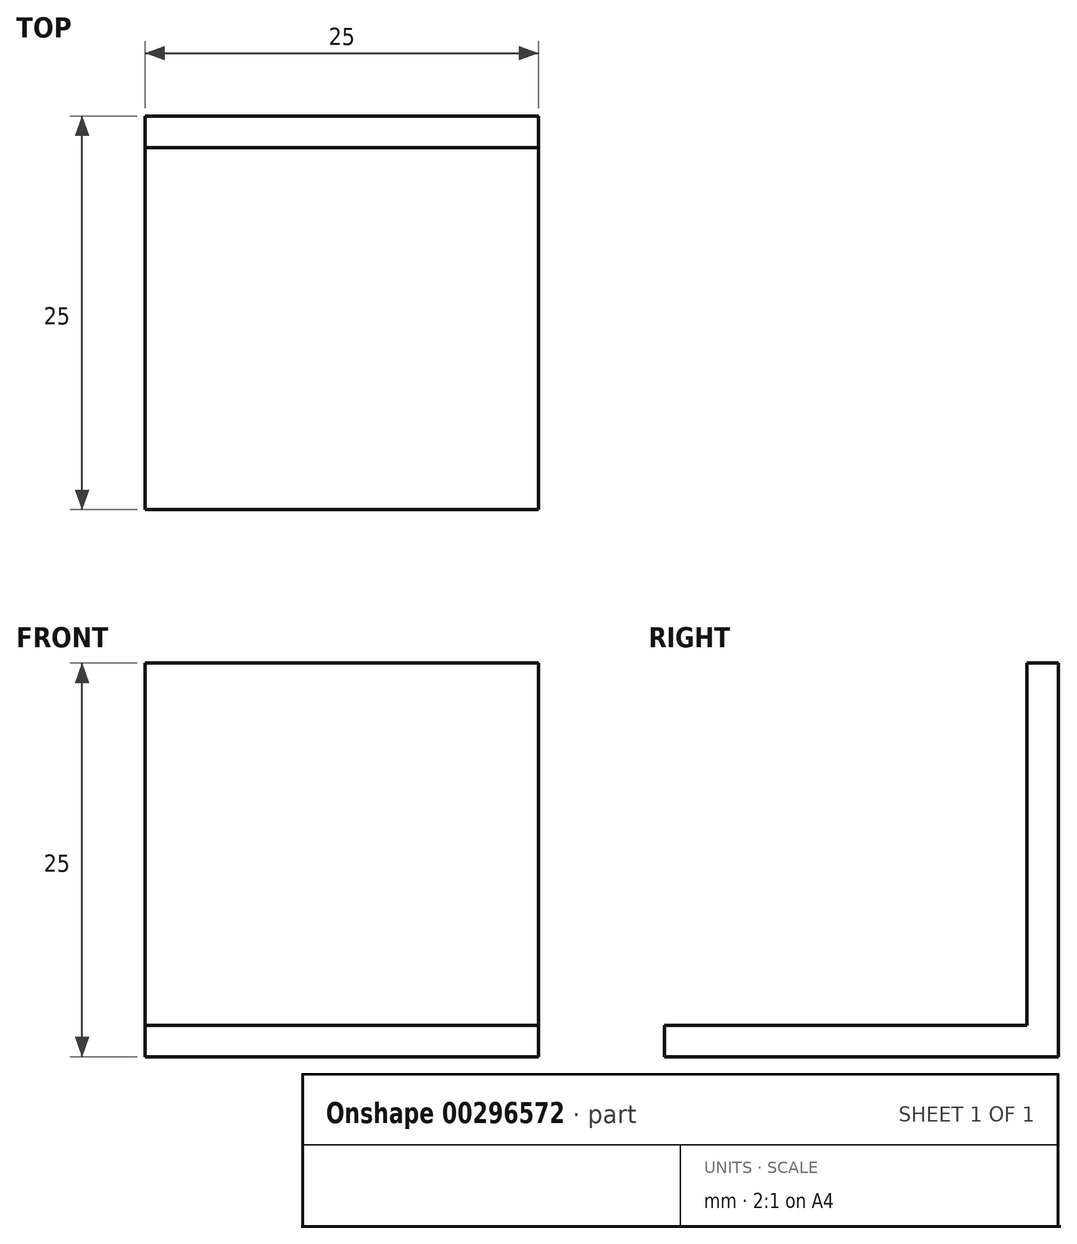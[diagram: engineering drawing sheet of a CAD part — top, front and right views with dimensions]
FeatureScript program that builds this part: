
annotation { "Feature Type Name" : "Feature", "Feature Type Description" : "" }
export const myFeature = defineFeature(function(context is Context, id is Id, definition is map)
    precondition{}
    {
        {
            var Q0;
            Q0=qCreatedBy(makeId("Top.planeOp"),FACE);
            var sketch = newSketch(context, id + "F0", { "sketchPlane" : qUnion([Q0])});
            skLineSegment(sketch, "E0.bottom", {"start": v(12.5, 12.5) * mm, "end": v(-12.5, 12.5) * mm});
            skLineSegment(sketch, "E0.top", {"start": v(12.5, -12.5) * mm, "end": v(-12.5, -12.5) * mm});
            skLineSegment(sketch, "E0.left", {"start": v(12.5, 12.5) * mm, "end": v(12.5, -12.5) * mm});
            skLineSegment(sketch, "E0.right", {"start": v(-12.5, 12.5) * mm, "end": v(-12.5, -12.5) * mm});
            skPoint(sketch, "E0.middle", {"position": v(0, 0) * mm});
            skLineSegment(sketch, "E1", {"start": v(-12.5, 10.5) * mm, "end": v(12.5, 10.5) * mm});
            skSolve(sketch);
        }
        {
            var Q0;
            {var subQ0=sQuery(id+"F0.wireOp",EDGE,"E0.top");Q0=makeQuery(id+"F0.imprint","IMPRINT",FACE,{"disambiguationData":[TD([[makeQuery(id+"F0.imprint","IMPRINT",EDGE,{"derivedFrom":subQ0}),-1.0]])]});}
            extrude(context, id + "F1", {"entities" : qUnion([Q0]), "depth" : 2 * mm});
        }
        {
            var Q0;
            {var subQ0=sQuery(id+"F0.wireOp",EDGE,"E0.bottom");Q0=makeQuery(id+"F0.imprint","IMPRINT",FACE,{"disambiguationData":[TD([[makeQuery(id+"F0.imprint","IMPRINT",EDGE,{"derivedFrom":subQ0}),1.0]])]});}
            extrude(context, id + "F2", {"entities" : qUnion([Q0]), "operationType" : NewBodyOperationType.ADD, "depth" : 25 * mm});
        }
    });
